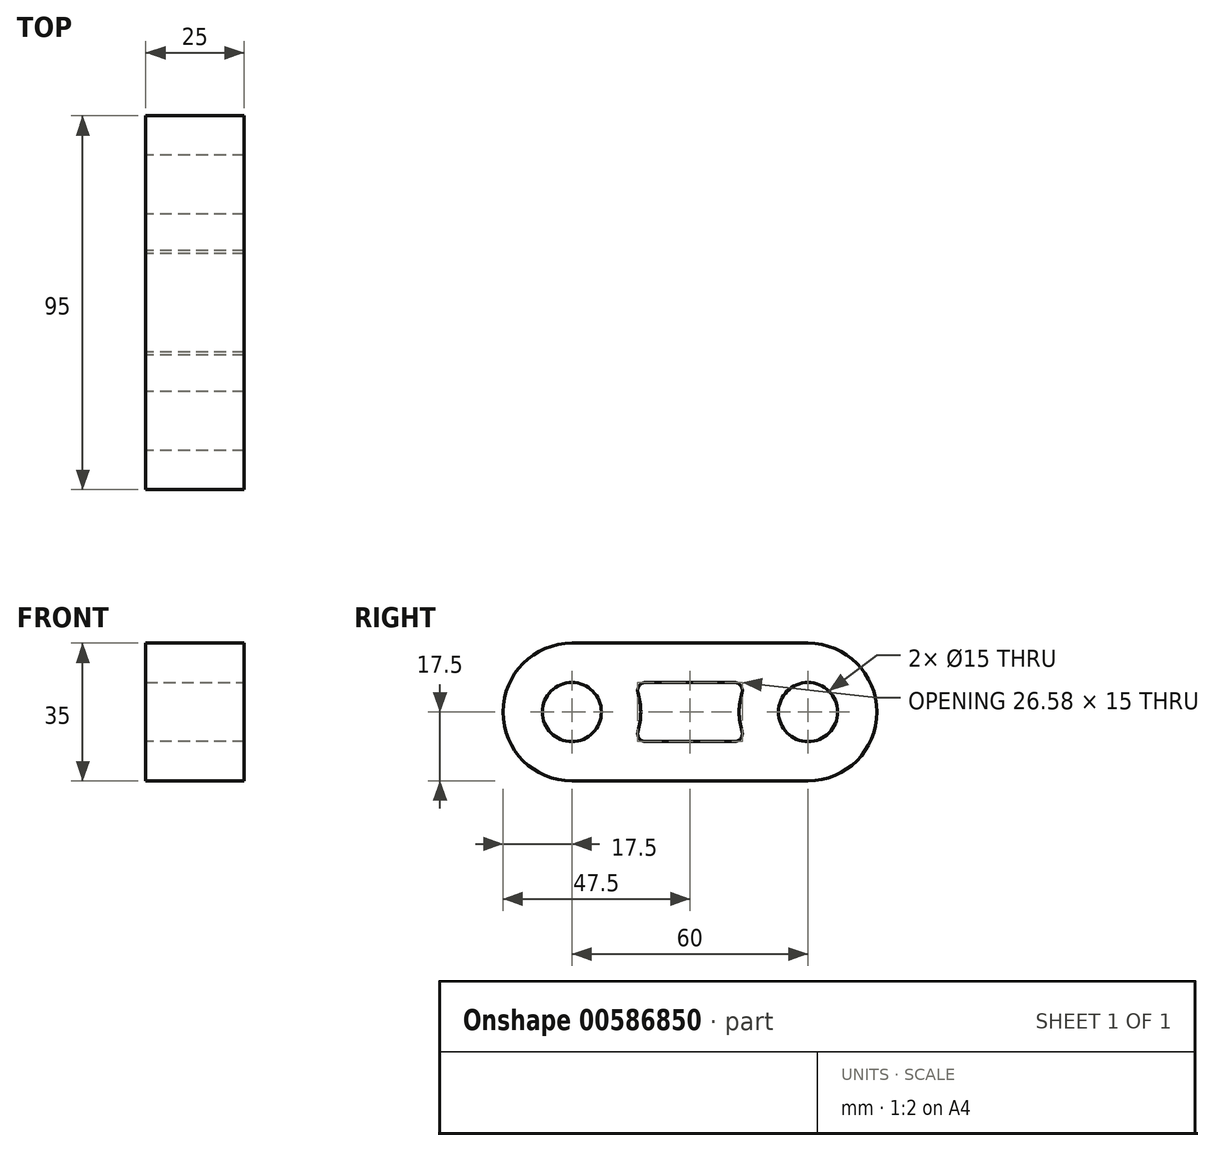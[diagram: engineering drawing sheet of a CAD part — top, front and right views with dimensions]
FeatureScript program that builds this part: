
annotation { "Feature Type Name" : "Feature", "Feature Type Description" : "" }
export const myFeature = defineFeature(function(context is Context, id is Id, definition is map)
    precondition{}
    {
        {
            var Q0;
            Q0=qCreatedBy(makeId("Right.planeOp"),FACE);
            var sketch = newSketch(context, id + "F0", { "sketchPlane" : qUnion([Q0])});
            skCircle(sketch, "E0", {"center": v(-30, 0) * mm, "radius": 7.5 * mm});
            skCircle(sketch, "E1", {"center": v(30, 0) * mm, "radius": 7.5 * mm});
            skArc(sketch, "E2", {"start": v(-30, 17.5) * mm, "mid": v(-47.5, 0) * mm, "end": v(-30, -17.5) * mm});
            skArc(sketch, "E3", {"start": v(14.19, 7.5) * mm, "mid": v(12.5, 0) * mm, "end": v(14.19, -7.5) * mm});
            skLineSegment(sketch, "E4.bottom", {"start": v(-30, 17.5) * mm, "end": v(30, 17.5) * mm});
            skLineSegment(sketch, "E4.top", {"start": v(-14.19, 7.5) * mm, "end": v(14.19, 7.5) * mm});
            skLineSegment(sketch, "E5", {"start": v(30, -17.5) * mm, "end": v(-30, -17.5) * mm});
            skLineSegment(sketch, "E6", {"start": v(-14.19, -7.5) * mm, "end": v(14.19, -7.5) * mm});
            skArc(sketch, "E7.trimOffspring", {"start": v(-14.19, -7.5) * mm, "mid": v(-12.5, 0) * mm, "end": v(-14.19, 7.5) * mm});
            skArc(sketch, "E8.trimOffspring", {"start": v(30, -17.5) * mm, "mid": v(47.5, 0) * mm, "end": v(30, 17.5) * mm});
            skSolve(sketch);
        }
        {
            var Q0;
            Q0=makeQuery(id+"F0.imprint","IMPRINT",FACE,{"disambiguationData":[TD([[makeQuery(id+"F0.imprint","IMPRINT",EDGE,{"derivedFrom":sQuery(id+"F0.wireOp",EDGE,"E0")}),-1.0]])]});
            extrude(context, id + "F1", {"entities" : qUnion([Q0]), "depth" : 25 * mm, "offsetDistance" : 25 * mm});
        }
        {
            var Q0;
            Q0=makeQuery(id+"F1.opExtrude","SWEPT_EDGE",EDGE,{"disambiguationData":[OSD([sQuery(id+"F0.wireOp",EDGE,"E4.top"),sQuery(id+"F0.wireOp",EDGE,"E7.trimOffspring")])]});
            var Q1;
            Q1=makeQuery(id+"F1.opExtrude","SWEPT_EDGE",EDGE,{"disambiguationData":[OSD([sQuery(id+"F0.wireOp",EDGE,"E6"),sQuery(id+"F0.wireOp",EDGE,"E7.trimOffspring")])]});
            var Q2;
            Q2=makeQuery(id+"F1.opExtrude","SWEPT_EDGE",EDGE,{"disambiguationData":[OSD([sQuery(id+"F0.wireOp",EDGE,"E3"),sQuery(id+"F0.wireOp",EDGE,"E6")])]});
            var Q3;
            Q3=makeQuery(id+"F1.opExtrude","SWEPT_EDGE",EDGE,{"disambiguationData":[OSD([sQuery(id+"F0.wireOp",EDGE,"E3"),sQuery(id+"F0.wireOp",EDGE,"E4.top")])]});
            fillet(context, id + "F2", {"entities" : qUnion([Q0, Q1, Q2, Q3]), "radius" : 2 * mm, "tangentPropagation" : true, "allowEdgeOverflow" : false});
        }
    });
